# Revit family: FantiniCosmi_BIM_CH193VMC
name_source: partatom
category: Generic Models
units: mm (PartAtom-declared; Revit-internal decimal feet)

## family parameters
Always vertical = Yes
Can host rebar = No
Cut with Voids When Loaded = No
Part Type = Normal
Room Calculation Point = No
Round Connector Dimension = Use Diameter
Shared = No
Work Plane-Based = No

## types (1)
- Standard
    Catalog web link = https://www.fantinicosmi.it
    Corrente assorbita = 150mA Max
    Default Elevation = 0 mm  [stored 0 ft]
    Description = Pannello remoto LCD per il controllo avanzato di impianti di ventilazione tramite VMC
    Designer = Carniti
    Dimensioni = 127 x 82 x 24 mm
    Grado di protezione = IP30
    IAQ = 5 LIVELLI
    Interfaccia di comunicazione = RS485
    Modalità di comunicazione = 9600bps, 8bit, nessuna parità, 1 bit stop
    Part Number = FantiniCosmi_BIM_CH193VMC
    Peso = 0,100 kg
    Rispondente alle Direttiva = 2014/30/UE (EMC) e Direttiva 2014/35/UE (LVD)
    Rispondenti alle norme = EN 60730-1 e parti seconde
    Scala di regolazione umidità relativa = 30÷70%
    Scala visualizzazione T ambiente = -50 ÷ +50°C
    Scala visualizzazione Umidità RH% = 0÷100%
    Spegnimento retroilluminazione = 60s da ultima pressione
    Temperatura di stoccaggio = -10°C ÷ +60°C
    Temperatura massima ambiente = 45°C
    Tensione nominale di alimentazione = 9 – 24Vcc
    Velocità ventole = 3 + BOOST
    risoluzione = 1%

note: [stored X ft] marks values corroborated as IEEE doubles in the binary element streams (Revit-internal decimal feet)

## geometry (parser evidence)
native form markers: Sweep x3
no freeform markers — native parametric forms only
